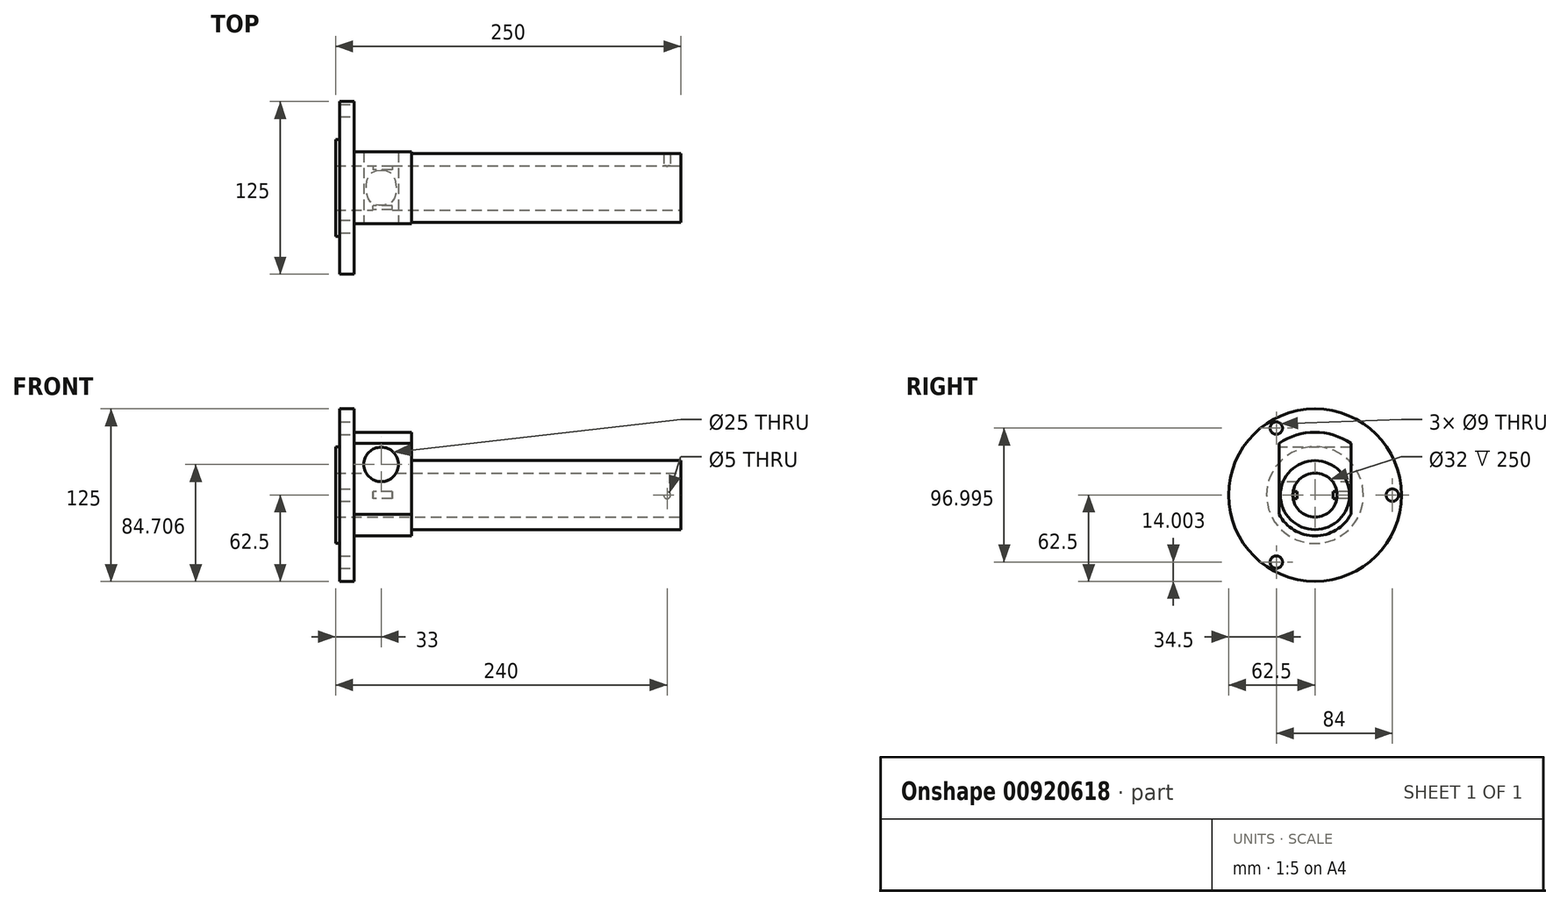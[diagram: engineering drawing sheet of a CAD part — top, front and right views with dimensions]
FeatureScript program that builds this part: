
annotation { "Feature Type Name" : "Feature", "Feature Type Description" : "" }
export const myFeature = defineFeature(function(context is Context, id is Id, definition is map)
    precondition{}
    {
        {
            var Q0;
            Q0=qCreatedBy(makeId("Front.planeOp"),FACE);
            var sketch = newSketch(context, id + "F0", { "sketchPlane" : qUnion([Q0])});
            skLineSegment(sketch, "E0", {"start": v(0, 62.5) * mm, "end": v(0, 35) * mm});
            skLineSegment(sketch, "E1", {"start": v(0, 35) * mm, "end": v(-3, 35) * mm});
            skLineSegment(sketch, "E2", {"start": v(-3, 35) * mm, "end": v(-3, 16) * mm});
            skLineSegment(sketch, "E3", {"start": v(-3, 16) * mm, "end": v(247, 16) * mm});
            skLineSegment(sketch, "E4", {"start": v(247, 16) * mm, "end": v(247, 25) * mm});
            skLineSegment(sketch, "E5", {"start": v(247, 25) * mm, "end": v(10.5, 25) * mm});
            skLineSegment(sketch, "E6", {"start": v(10.5, 25) * mm, "end": v(10.5, 62.5) * mm});
            skLineSegment(sketch, "E7", {"start": v(0, 62.5) * mm, "end": v(10.5, 62.5) * mm});
            skLineSegment(sketch, "E8", {"start": v(0, 0) * mm, "end": v(-22.5, 0) * mm, "construction": true});
            skSolve(sketch);
        }
        {
            var Q0;
            Q0=makeQuery(id+"F0.imprint","IMPRINT",FACE,{"disambiguationData":[TD([[makeQuery(id+"F0.imprint","IMPRINT",EDGE,{"derivedFrom":sQuery(id+"F0.wireOp",EDGE,"E0")}),1.0]])]});
            var Q1;
            Q1=sQuery(id+"F0.wireOp",EDGE,"E8");
            revolve(context, id + "F1", {"surfaceOperationType" : NewSurfaceOperationType.NEW, "entities" : qUnion([Q0]), "axis" : qUnion([Q1]), "revolveType" : RevolveType.FULL});
        }
        {
            var Q0;
            Q0=makeQuery(id+"F1.opRevolve","SWEPT_FACE",FACE,{"disambiguationData":[OSD([sQuery(id+"F0.wireOp",EDGE,"E6")])]});
            var sketch = newSketch(context, id + "F2", { "sketchPlane" : qUnion([Q0])});
            skArc(sketch, "E9", {"start": v(26, 37.34) * mm, "mid": v(0, 45.5) * mm, "end": v(-26, 37.34) * mm});
            skLineSegment(sketch, "E10", {"start": v(-26, 37.34) * mm, "end": v(-26, -13.94) * mm});
            skLineSegment(sketch, "E11", {"start": v(26, 37.34) * mm, "end": v(26, -13.94) * mm});
            skArc(sketch, "E12", {"start": v(-26, -13.94) * mm, "mid": v(0, -29.5) * mm, "end": v(26, -13.94) * mm});
            skCircle(sketch, "E13", {"center": v(0, 0) * mm, "radius": 25 * mm});
            skSolve(sketch);
        }
        {
            var Q0;
            Q0=makeQuery(id+"F2.imprint","IMPRINT",FACE,{"disambiguationData":[TD([[makeQuery(id+"F2.imprint","IMPRINT",EDGE,{"derivedFrom":sQuery(id+"F2.wireOp",EDGE,"E9")}),1.0]])]});
            extrude(context, id + "F3", {"entities" : qUnion([Q0]), "operationType" : NewBodyOperationType.ADD, "depth" : (55 - 13.5) * mm, "offsetDistance" : 25 * mm});
        }
        {
            var Q0;
            Q0=qCreatedBy(makeId("Front.planeOp"),FACE);
            var sketch = newSketch(context, id + "F4", { "sketchPlane" : qUnion([Q0])});
            skCircle(sketch, "E14", {"center": v(30, 22.2) * mm, "radius": 12.5 * mm});
            skSolve(sketch);
        }
        {
            var Q0;
            Q0=makeQuery(id+"F4.imprint","IMPRINT",FACE,{"disambiguationData":[TD([[makeQuery(id+"F4.imprint","IMPRINT",EDGE,{"derivedFrom":sQuery(id+"F4.wireOp",EDGE,"E14")}),1.0]])]});
            extrude(context, id + "F5", {"entities" : qUnion([Q0]), "operationType" : NewBodyOperationType.REMOVE, "oppositeDirection" : true, "depth" : 60 * mm, "offsetDistance" : 25 * mm, "symmetric" : true});
        }
        {
            var Q0;
            Q0=qCreatedBy(makeId("Front.planeOp"),FACE);
            var sketch = newSketch(context, id + "F6", { "sketchPlane" : qUnion([Q0])});
            skCircle(sketch, "E15", {"center": v(237, 0) * mm, "radius": 2.5 * mm});
            skSolve(sketch);
        }
        {
            var Q0;
            Q0=makeQuery(id+"F6.imprint","IMPRINT",FACE,{"disambiguationData":[TD([[makeQuery(id+"F6.imprint","IMPRINT",EDGE,{"derivedFrom":sQuery(id+"F6.wireOp",EDGE,"E15")}),1.0]])]});
            extrude(context, id + "F7", {"entities" : qUnion([Q0]), "operationType" : NewBodyOperationType.REMOVE, "endBound" : BoundingType.THROUGH_ALL, "oppositeDirection" : true, "depth" : 25 * mm, "offsetDistance" : 25 * mm});
        }
        {
            var Q0;
            Q0=makeQuery(id+"F1.opRevolve","SWEPT_FACE",FACE,{"disambiguationData":[OSD([sQuery(id+"F0.wireOp",EDGE,"E6")])]});
            var sketch = newSketch(context, id + "F8", { "sketchPlane" : qUnion([Q0])});
            skCircle(sketch, "E16", {"center": v(0, 0) * mm, "radius": 56 * mm, "construction": true});
            skLineSegment(sketch, "E17", {"start": v(0, 0) * mm, "end": v(56, 0) * mm, "construction": true});
            skLineSegment(sketch, "E18", {"start": v(0, 0) * mm, "end": v(-28, 48.5) * mm, "construction": true});
            skLineSegment(sketch, "E19", {"start": v(0, 0) * mm, "end": v(-28, -48.5) * mm, "construction": true});
            skCircle(sketch, "E20", {"center": v(-28, 48.5) * mm, "radius": 4.5 * mm});
            skCircle(sketch, "E21", {"center": v(-28, -48.5) * mm, "radius": 4.5 * mm});
            skCircle(sketch, "E22", {"center": v(56, 0) * mm, "radius": 4.5 * mm});
            skSolve(sketch);
        }
        {
            var Q0;
            Q0=makeQuery(id+"F8.imprint","IMPRINT",FACE,{"disambiguationData":[TD([[makeQuery(id+"F8.imprint","IMPRINT",EDGE,{"derivedFrom":sQuery(id+"F8.wireOp",EDGE,"E20")}),1.0]])]});
            var Q1;
            Q1=makeQuery(id+"F8.imprint","IMPRINT",FACE,{"disambiguationData":[TD([[makeQuery(id+"F8.imprint","IMPRINT",EDGE,{"derivedFrom":sQuery(id+"F8.wireOp",EDGE,"E22")}),1.0]])]});
            var Q2;
            Q2=makeQuery(id+"F8.imprint","IMPRINT",FACE,{"disambiguationData":[TD([[makeQuery(id+"F8.imprint","IMPRINT",EDGE,{"derivedFrom":sQuery(id+"F8.wireOp",EDGE,"E21")}),1.0]])]});
            extrude(context, id + "F9", {"entities" : qUnion([Q0, Q1, Q2]), "operationType" : NewBodyOperationType.REMOVE, "endBound" : BoundingType.THROUGH_ALL, "oppositeDirection" : true, "depth" : 25 * mm, "offsetDistance" : 25 * mm});
        }
        {
            var Q0;
            Q0=makeQuery(id+"F1.opRevolve","SWEPT_FACE",FACE,{"disambiguationData":[OSD([sQuery(id+"F0.wireOp",EDGE,"E2")])]});
            cPlane(context, id + "F10", {"entities" : qUnion([Q0]), "cplaneType" : CPlaneType.OFFSET, "offset" : 27 * mm, "oppositeDirection" : true, "width" : 150 * mm, "height" : 150 * mm});
        }
        {
            var Q0;
            Q0=qCreatedBy(id+"F10.planeOp",FACE);
            var sketch = newSketch(context, id + "F11", { "sketchPlane" : qUnion([Q0])});
            skArc(sketch, "E23.0", {"start": v(-15.8, 2.5) * mm, "mid": v(-16, 0) * mm, "end": v(-15.8, -2.5) * mm});
            skLineSegment(sketch, "E24", {"start": v(-15.8, -2.5) * mm, "end": v(-13, -2.5) * mm});
            skLineSegment(sketch, "E25", {"start": v(-13, -2.5) * mm, "end": v(-13, 2.5) * mm});
            skLineSegment(sketch, "E26", {"start": v(-15.8, 2.5) * mm, "end": v(-13, 2.5) * mm});
            skLineSegment(sketch, "E27", {"start": v(15.8, 2.5) * mm, "end": v(13, 2.5) * mm});
            skLineSegment(sketch, "E28", {"start": v(13, 2.5) * mm, "end": v(13, -2.5) * mm});
            skLineSegment(sketch, "E29", {"start": v(13, -2.5) * mm, "end": v(15.8, -2.5) * mm});
            skArc(sketch, "E30.trimOffspring", {"start": v(15.8, -2.5) * mm, "mid": v(16, 0) * mm, "end": v(15.8, 2.5) * mm});
            skSolve(sketch);
        }
        {
            var Q0;
            Q0=makeQuery(id+"F11.imprint","IMPRINT",FACE,{"disambiguationData":[TD([[makeQuery(id+"F11.imprint","IMPRINT",EDGE,{"derivedFrom":sQuery(id+"F11.wireOp",EDGE,"E23.0")}),1.0]])]});
            var Q1;
            Q1=makeQuery(id+"F11.imprint","IMPRINT",FACE,{"disambiguationData":[TD([[makeQuery(id+"F11.imprint","IMPRINT",EDGE,{"derivedFrom":sQuery(id+"F11.wireOp",EDGE,"E27")}),1.0]])]});
            extrude(context, id + "F12", {"entities" : qUnion([Q0, Q1]), "operationType" : NewBodyOperationType.ADD, "oppositeDirection" : true, "depth" : 14 * mm, "offsetDistance" : 25 * mm});
        }
    });
